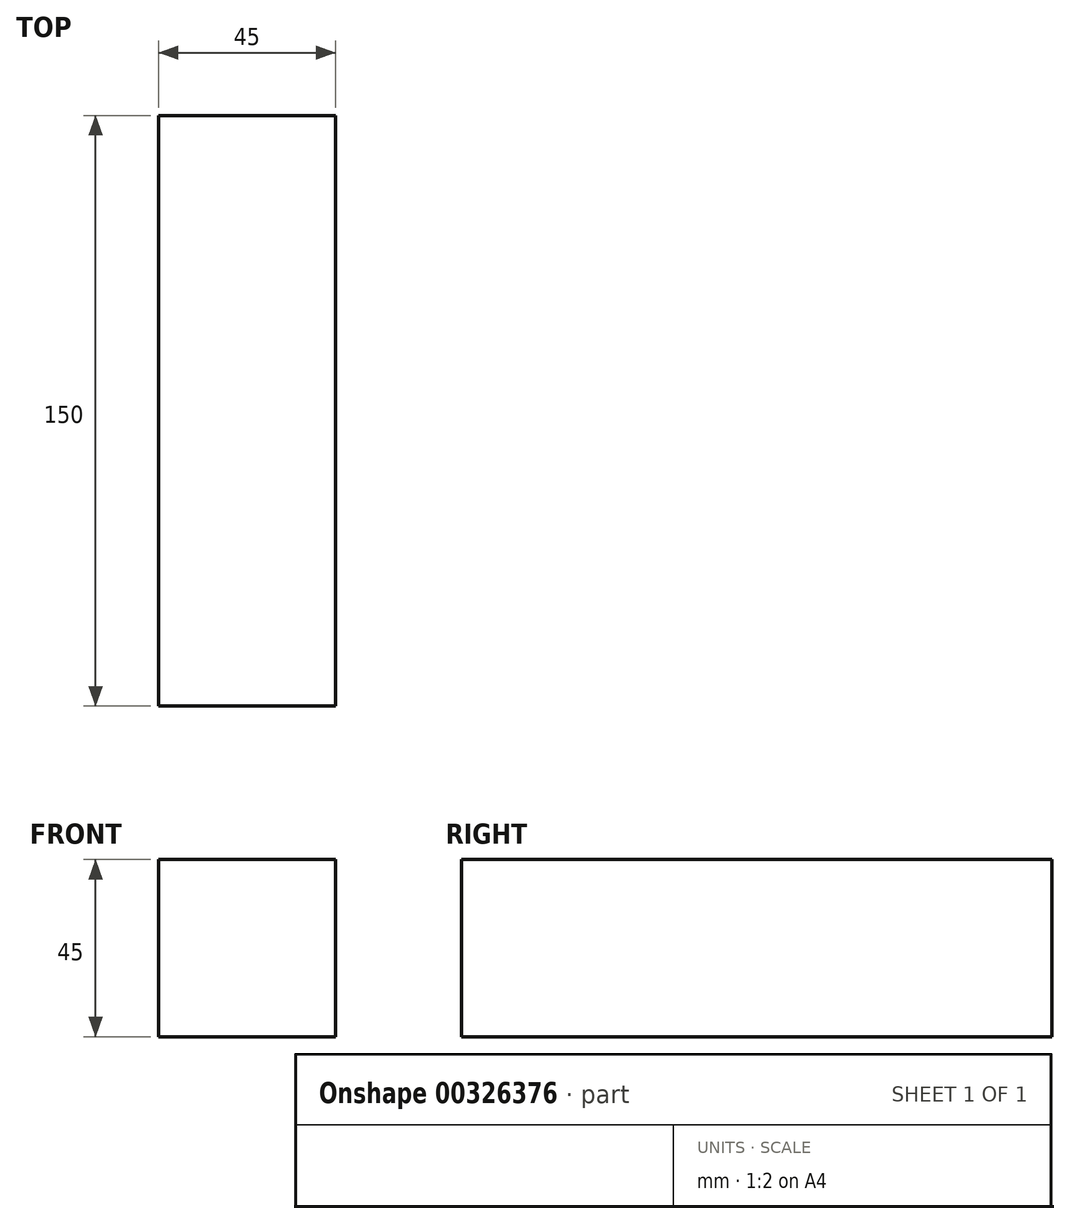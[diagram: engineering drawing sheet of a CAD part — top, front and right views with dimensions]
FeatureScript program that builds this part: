
annotation { "Feature Type Name" : "Feature", "Feature Type Description" : "" }
export const myFeature = defineFeature(function(context is Context, id is Id, definition is map)
    precondition{}
    {
        {
            var Q0;
            Q0=qCreatedBy(makeId("Front.planeOp"),FACE);
            var sketch = newSketch(context, id + "F0", { "sketchPlane" : qUnion([Q0])});
            skLineSegment(sketch, "E0.bottom", {"start": v(0, 0) * mm, "end": v(45, 0) * mm});
            skLineSegment(sketch, "E0.top", {"start": v(0, 45) * mm, "end": v(45, 45) * mm});
            skLineSegment(sketch, "E0.left", {"start": v(0, 0) * mm, "end": v(0, 45) * mm});
            skLineSegment(sketch, "E0.right", {"start": v(45, 0) * mm, "end": v(45, 45) * mm});
            skSolve(sketch);
        }
        {
            var Q0;
            Q0=makeQuery(id+"F0.imprint","IMPRINT",FACE,{"disambiguationData":[TD([[makeQuery(id+"F0.imprint","IMPRINT",EDGE,{"derivedFrom":sQuery(id+"F0.wireOp",EDGE,"E0.bottom")}),1.0]])]});
            extrude(context, id + "F1", {"entities" : qUnion([Q0]), "depth" : 150 * mm});
        }
    });
